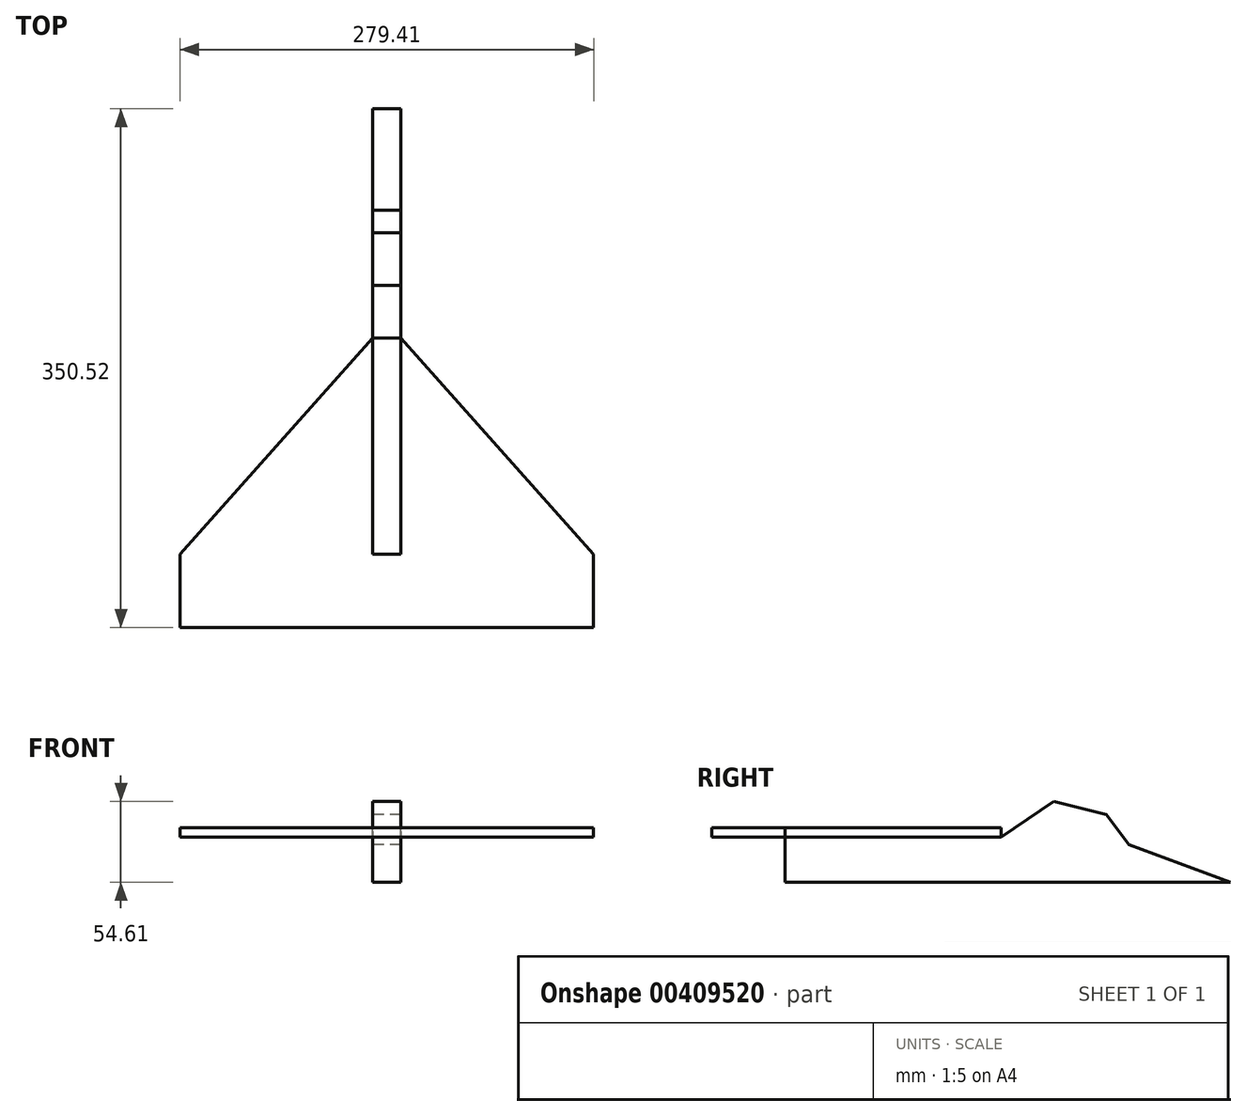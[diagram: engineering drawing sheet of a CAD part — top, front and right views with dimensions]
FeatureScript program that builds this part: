
annotation { "Feature Type Name" : "Feature", "Feature Type Description" : "" }
export const myFeature = defineFeature(function(context is Context, id is Id, definition is map)
    precondition{}
    {
        {
            var Q0;
            Q0=qCreatedBy(makeId("Right.planeOp"),FACE);
            var sketch = newSketch(context, id + "F0", { "sketchPlane" : qUnion([Q0])});
            skLineSegment(sketch, "E0", {"start": v(-237.75, 0) * mm, "end": v(234.84, 0) * mm, "construction": true});
            skLineSegment(sketch, "E1", {"start": v(-237.75, 0) * mm, "end": v(-237.75, 30.48) * mm});
            skLineSegment(sketch, "E2", {"start": v(-237.75, 30.48) * mm, "end": v(-91.7, 30.48) * mm});
            skLineSegment(sketch, "E3", {"start": v(-91.7, 30.48) * mm, "end": v(-56.14, 54.6) * mm});
            skLineSegment(sketch, "E4", {"start": v(-56.14, 54.6) * mm, "end": v(-20.58, 45.72) * mm});
            skLineSegment(sketch, "E5", {"start": v(-20.58, 45.72) * mm, "end": v(-5.34, 25.4) * mm});
            skLineSegment(sketch, "E6", {"start": v(-5.34, 25.4) * mm, "end": v(63.24, 0) * mm});
            skLineSegment(sketch, "E7", {"start": v(63.24, 0) * mm, "end": v(-237.75, 0) * mm});
            skSolve(sketch);
        }
        {
            var Q0;
            Q0=makeQuery(id+"F0.imprint","IMPRINT",FACE,{"disambiguationData":[TD([[makeQuery(id+"F0.imprint","IMPRINT",EDGE,{"derivedFrom":sQuery(id+"F0.wireOp",EDGE,"E1")}),-1.0]])]});
            extrude(context, id + "F1", {"entities" : qUnion([Q0]), "depth" : 19.05 * mm});
        }
        {
            var Q0;
            Q0=makeQuery(id+"F0.imprint","IMPRINT",FACE,{"disambiguationData":[TD([[makeQuery(id+"F0.imprint","IMPRINT",EDGE,{"derivedFrom":sQuery(id+"F0.wireOp",EDGE,"E1")}),-1.0]])]});
            extrude(context, id + "F2", {"entities" : qUnion([Q0]), "depth" : 19.05 * mm});
        }
        {
            var Q0;
            Q0=makeQuery(id+"F2.opExtrude","SWEPT_FACE",FACE,{"disambiguationData":[OSD([sQuery(id+"F0.wireOp",EDGE,"E2")])]});
            var sketch = newSketch(context, id + "F3", { "sketchPlane" : qUnion([Q0])});
            skLineSegment(sketch, "E8", {"start": v(149.22, -287.28) * mm, "end": v(149.22, -237.75) * mm});
            skLineSegment(sketch, "E9", {"start": v(149.23, -237.75) * mm, "end": v(19.05, -91.7) * mm});
            skLineSegment(sketch, "E10", {"start": v(19.05, -91.7) * mm, "end": v(0, -91.7) * mm});
            skLineSegment(sketch, "E11", {"start": v(0, -91.7) * mm, "end": v(-130.18, -237.75) * mm});
            skLineSegment(sketch, "E12", {"start": v(-130.18, -237.75) * mm, "end": v(-130.18, -287.28) * mm});
            skLineSegment(sketch, "E13", {"start": v(149.22, -287.28) * mm, "end": v(-130.17, -287.28) * mm});
            skLineSegment(sketch, "E14", {"start": v(-130.18, -287.28) * mm, "end": v(-130.18, -237.75) * mm});
            skSolve(sketch);
        }
        {
            var Q0;
            Q0=makeQuery(id+"F3.imprint","IMPRINT",FACE,{"disambiguationData":[TD([[makeQuery(id+"F3.imprint","IMPRINT",EDGE,{"derivedFrom":sQuery(id+"F3.wireOp",EDGE,"E8")}),1.0]])]});
            extrude(context, id + "F4", {"entities" : qUnion([Q0]), "depth" : 6.35 * mm});
        }
    });
